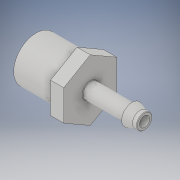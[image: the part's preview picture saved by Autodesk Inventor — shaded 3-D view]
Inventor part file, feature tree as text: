
AUTODESK INVENTOR PART (.ipt)
format: ipt  version: 2019.4 (Build 234330000, 330)  size: 2,636,800 bytes
history: native  units: mm
features: fillet x1
ambient origin geometry x8: Origin, YZ Plane, XZ Plane, XY Plane, X Axis, Y Axis, Z Axis, Center Point
bodies: Solid1 (feature_tree)
feature tree (1):
  fillet  "Fillet2"  [1 undecoded]
note: 1 required parameter value undecoded (feature->parameter linkage not recoverable at this tier; creation-order binding heuristic only, values carry confidence <= 0.55)
